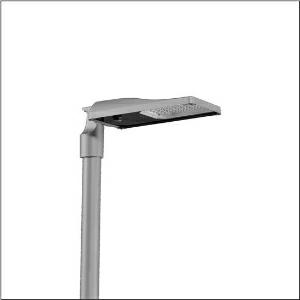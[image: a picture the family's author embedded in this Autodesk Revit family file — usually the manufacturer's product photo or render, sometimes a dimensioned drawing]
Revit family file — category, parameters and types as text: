
# Revit family: streetlight_sl_31_mini___st1_0a_5xh6d31r08ga_9a85
name_source: partatom
category: Lighting Fixtures
units: mm (PartAtom-declared; Revit-internal decimal feet)

## family parameters
Cut with Voids When Loaded = No
Host = Face
Light Source = No
Part Type = Normal
Room Calculation Point = No
Round Connector Dimension = Use Diameter
Shared = No

## types (1)
- --- (1 x LED, 5880 lm, 39.3 W, 3000K)
    Apparent Load = 39 VA
    CIE Flux Codes = 37 72 97 100 100
    Color Rendering = 70
    Color Temperature = 3000K
    Default Elevation = 1800 mm
    Description = Streetlight SL 31 mini D4i, Desk-Remote mast luminaire for post-top, side-entry; light control with lens of PMMA; light distribution: ST1.0a, direct asymmetric distribution, for standard-compliant lighting for roads and squares; LED: luminous flux: 5.880lm, light colour: 730, colour temperature: 3000K; luminous efficacy: 149,6lm/W; control: pre-setting: logarithmic dimming characteristic, flexible luminous flux parameterisation, time-dependent luminous flux control, constant luminous flux control, power reduction, intelligent temperature release in ECG and LED module, overheat protection; luminaire housing, of diecast aluminium, Siteco® metallic grey (DB 702S), corrosivity category C5 high according to DIN EN ISO 12944; cover of toughened safety glass, transparent, opened without tools; mast flange of diecast aluminium, Siteco® metallic grey (DB 702S), spigot size: 76/60mm, mast flange included unmounted; with cable H07RN-F 2x 1.5mm², cable length: 6,5m, connection cable pre-assembled; mains connection: 220..240V, AC, 50/60Hz; power consumption (at start of service life): 39,3W / (at end of service life): 40,7W / (with reduced operation 50%): 18,1W; protection rating (complete): IP66; insulation class (complete): insulation class II (safety insulation); impact resistance: IK09; certification: CE, ENEC, ENEC+, VDE, UKCA, ZD4i; permissible operating ambient temperature for outdoor applications: -40..+50°C; packaging unit: 1 piece

Light Distribution: ST1.0a
    Height = 76 mm
    Lamp = 1 x LED
    Lamp Light Flux = 5880 lm
    Lamp Power = 39.3 W
    Lamp count = 1
    Length = 547 mm
    Luminous efficacy = 150 lm/W
    Manufacturer = Siteco
    ModVariant = No
    Model = 5XH6D31R08GA
    Number of Poles = 1
    OnlyDefault = Yes
    Power Factor = 1
    Product Name = Streetlight SL 31 mini | ST1.0a
    Product group = mast luminaire | pylon top
    ProductGroupID = 6100
    Protection Class = Protection class II
    Protection Degree = IP 66
    RLX_Detail_Level = 1
    RLX_Emergency_Light_Flux = 0 lm
    RLX_Emergency_Type = 0
    RLX_Emergency_Type_DB = No
    RlxData = <blob elided: 39717 chars, md5=26c74f55>
    Socket = socket
    Standby Power = 0 W
    System Light Flux = 5880 lm
    System Power = 39 W
    Type Comments = factory setting: luminous flux: 100 % | dim-lin: 254 | 798 mA
    Type Image = l_1300328.jpg
    URL = http://relux.com
    VarID = @adj_054076
    Voltage = 0 V
    Weight = 0.00 kg
    Width = 265 mm

## geometry (parser evidence)
native form markers: Blend x4, Sweep x10
no freeform markers — native parametric forms only
